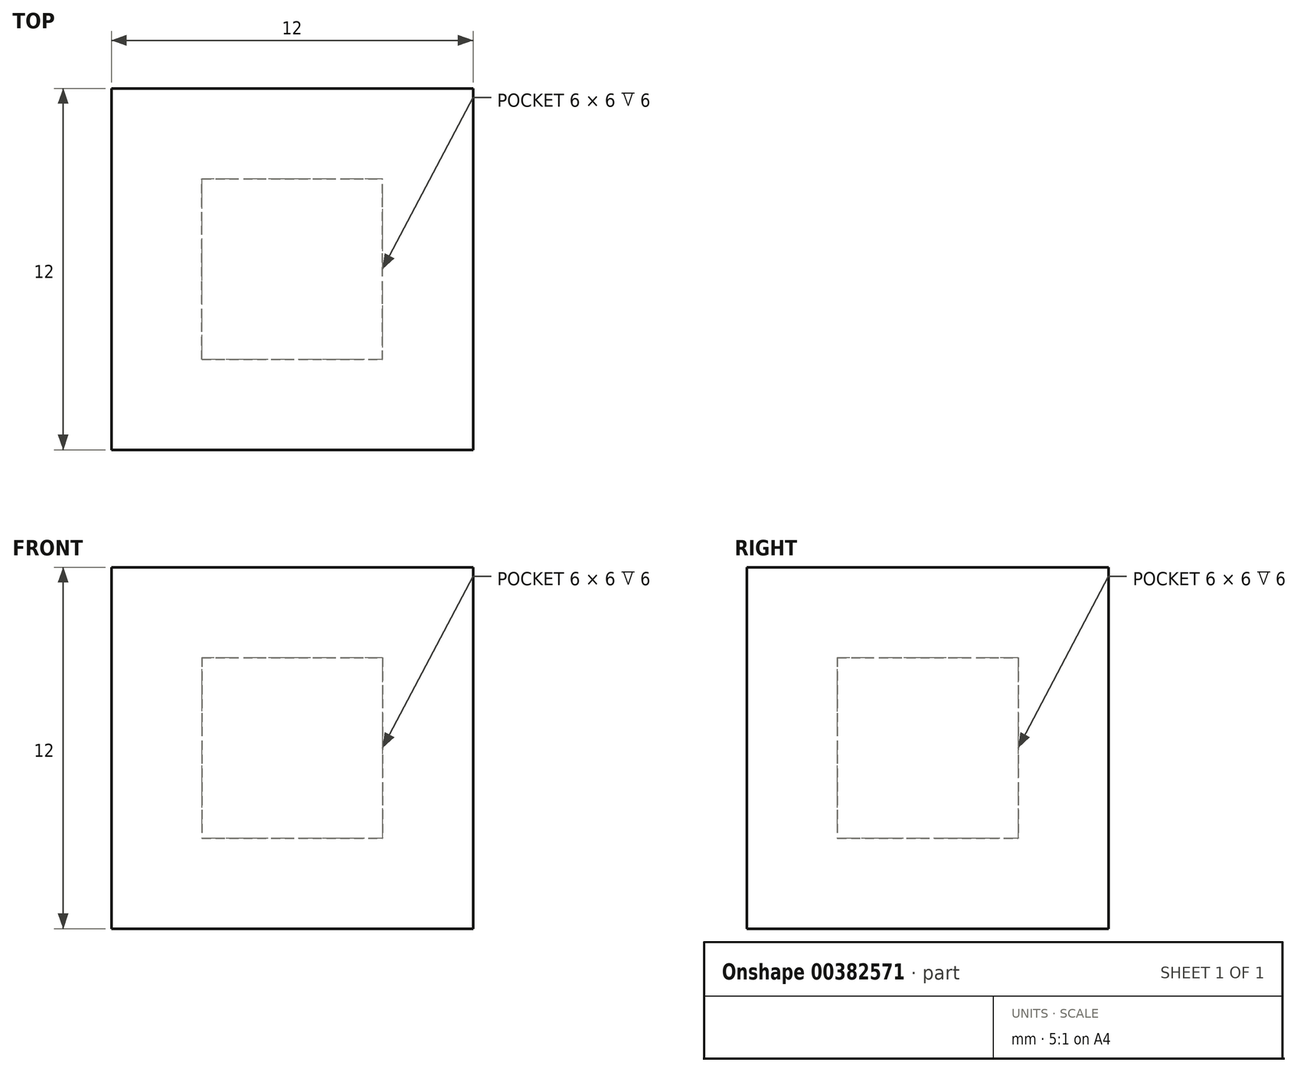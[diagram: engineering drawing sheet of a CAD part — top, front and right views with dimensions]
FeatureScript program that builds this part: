
annotation { "Feature Type Name" : "Feature", "Feature Type Description" : "" }
export const myFeature = defineFeature(function(context is Context, id is Id, definition is map)
    precondition{}
    {
        {
            var Q0;
            Q0=qCreatedBy(makeId("Top.planeOp"),FACE);
            var sketch = newSketch(context, id + "F0", { "sketchPlane" : qUnion([Q0])});
            skLineSegment(sketch, "E0.bottom", {"start": v(-12, 0) * mm, "end": v(0, 0) * mm});
            skLineSegment(sketch, "E0.top", {"start": v(-12, -12) * mm, "end": v(0, -12) * mm});
            skLineSegment(sketch, "E0.left", {"start": v(-12, 0) * mm, "end": v(-12, -12) * mm});
            skLineSegment(sketch, "E0.right", {"start": v(0, 0) * mm, "end": v(0, -12) * mm});
            skSolve(sketch);
        }
        {
            var Q0;
            Q0 = qSketchRegion(id + "F0", true);
            var Q1;
            Q1=makeQuery(id+"F0.imprint","IMPRINT",FACE,{"disambiguationData":[TD([[makeQuery(id+"F0.imprint","IMPRINT",EDGE,{"derivedFrom":sQuery(id+"F0.wireOp",EDGE,"E0.bottom")}),-1.0]])]});
            extrude(context, id + "F1", {"entities" : qUnion([Q0, Q1]), "depth" : 12 * mm});
        }
        {
            var Q0;
            Q0=qCreatedBy(makeId("Top.planeOp"),FACE);
            var sketch = newSketch(context, id + "F2", { "sketchPlane" : qUnion([Q0])});
            skLineSegment(sketch, "E1.bottom", {"start": v(0, 0) * mm, "end": v(-3, 0) * mm, "construction": true});
            skLineSegment(sketch, "E1.top", {"start": v(0, -3) * mm, "end": v(-3, -3) * mm, "construction": true});
            skLineSegment(sketch, "E1.left", {"start": v(0, 0) * mm, "end": v(0, -3) * mm, "construction": true});
            skLineSegment(sketch, "E1.right", {"start": v(-3, 0) * mm, "end": v(-3, -3) * mm, "construction": true});
            skLineSegment(sketch, "E2.bottom", {"start": v(-12, -12) * mm, "end": v(-9, -12) * mm, "construction": true});
            skLineSegment(sketch, "E2.top", {"start": v(-12, -9) * mm, "end": v(-9, -9) * mm, "construction": true});
            skLineSegment(sketch, "E2.left", {"start": v(-12, -12) * mm, "end": v(-12, -9) * mm, "construction": true});
            skLineSegment(sketch, "E2.right", {"start": v(-9, -12) * mm, "end": v(-9, -9) * mm, "construction": true});
            skLineSegment(sketch, "E3.bottom", {"start": v(-9, -9) * mm, "end": v(-3, -9) * mm});
            skLineSegment(sketch, "E3.top", {"start": v(-9, -3) * mm, "end": v(-3, -3) * mm});
            skLineSegment(sketch, "E3.left", {"start": v(-9, -9) * mm, "end": v(-9, -3) * mm});
            skLineSegment(sketch, "E3.right", {"start": v(-3, -9) * mm, "end": v(-3, -3) * mm});
            skSolve(sketch);
        }
        {
            var Q0;
            Q0=makeQuery(id+"F2.imprint","IMPRINT",FACE,{"disambiguationData":[TD([[makeQuery(id+"F2.imprint","IMPRINT",EDGE,{"derivedFrom":sQuery(id+"F2.wireOp",EDGE,"E3.bottom")}),1.0]])]});
            extrude(context, id + "F3", {"entities" : qUnion([Q0]), "operationType" : NewBodyOperationType.REMOVE, "depth" : 9 * mm, "hasSecondDirection" : true, "secondDirectionOppositeDirection" : true, "secondDirectionDepth" : -3 * mm});
        }
    });
